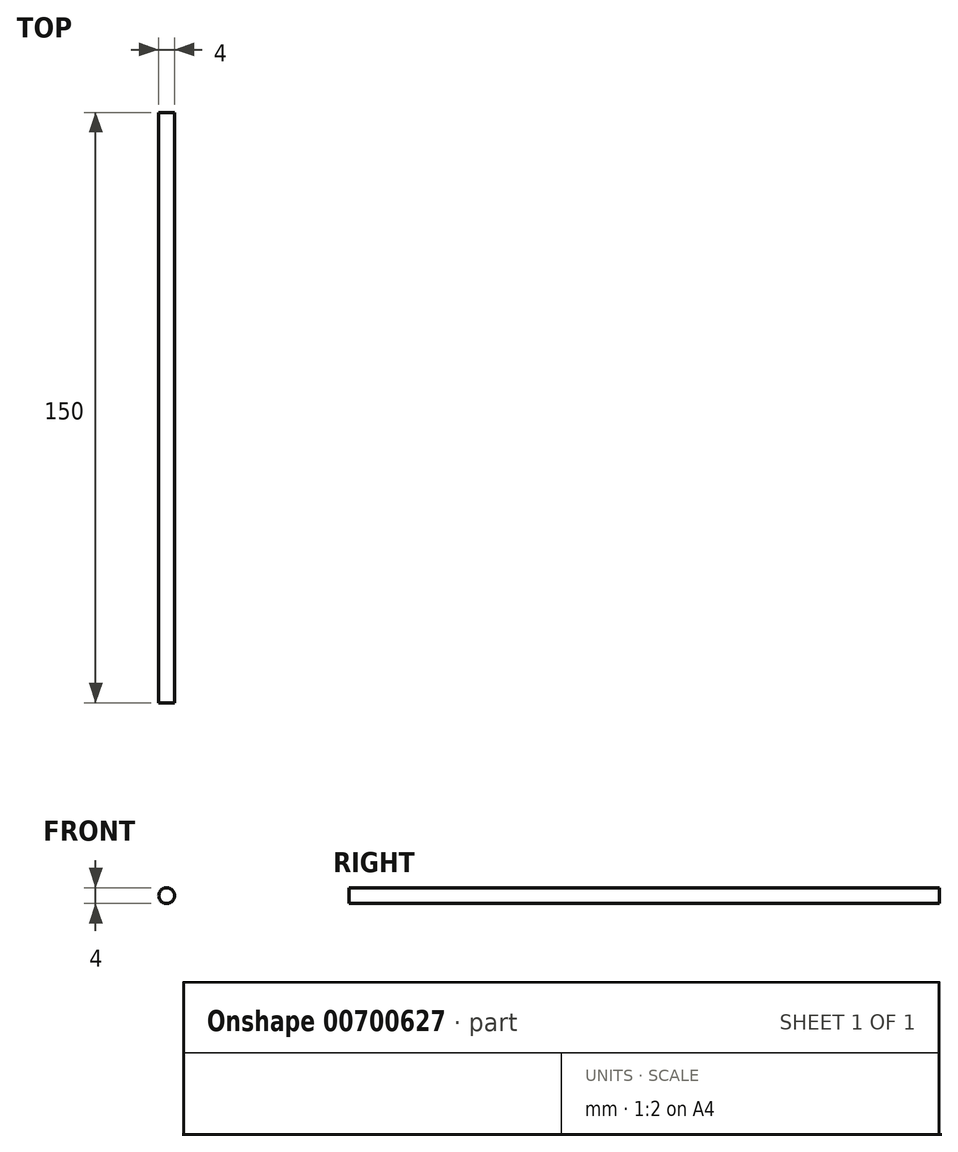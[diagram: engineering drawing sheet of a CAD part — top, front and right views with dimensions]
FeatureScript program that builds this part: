
annotation { "Feature Type Name" : "Feature", "Feature Type Description" : "" }
export const myFeature = defineFeature(function(context is Context, id is Id, definition is map)
    precondition{}
    {
        {
            var Q0;
            Q0=qCreatedBy(makeId("Front.planeOp"),FACE);
            var sketch = newSketch(context, id + "F0", { "sketchPlane" : qUnion([Q0])});
            skCircle(sketch, "E0", {"center": v(0, 0) * mm, "radius": 2 * mm});
            skSolve(sketch);
        }
        {
            var Q0;
            Q0=qSketchRegion(id+"F0",true);
            extrude(context, id + "F1", {"entities" : qUnion([Q0]), "depth" : 150 * mm, "offsetDistance" : 25 * mm});
        }
    });
